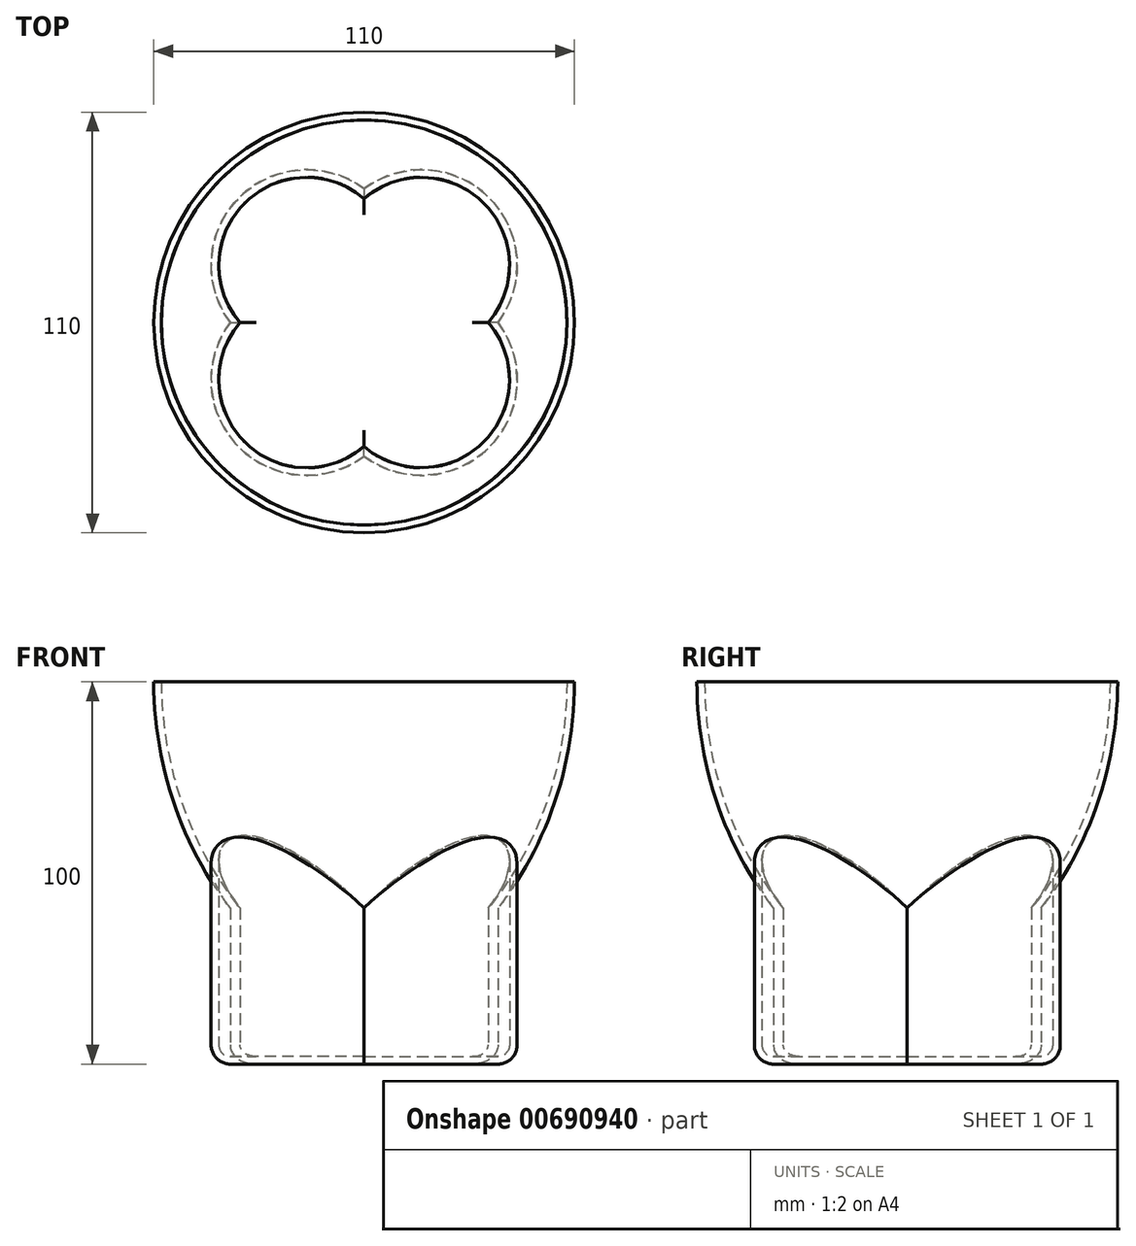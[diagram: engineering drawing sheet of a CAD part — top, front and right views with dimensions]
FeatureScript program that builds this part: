
annotation { "Feature Type Name" : "Feature", "Feature Type Description" : "" }
export const myFeature = defineFeature(function(context is Context, id is Id, definition is map)
    precondition{}
    {
        {
            var Q0;
            Q0=qCreatedBy(makeId("Top.planeOp"),FACE);
            var sketch = newSketch(context, id + "F0", { "sketchPlane" : qUnion([Q0])});
            skArc(sketch, "E0", {"start": v(0, 35) * mm, "mid": v(-32.68, 32.68) * mm, "end": v(-35, 0) * mm});
            skArc(sketch, "E1.MirrorC", {"start": v(0, 35) * mm, "mid": v(32.68, 32.68) * mm, "end": v(35, 0) * mm});
            skArc(sketch, "E2.trimOffspring", {"start": v(0, -35) * mm, "mid": v(-32.68, -32.68) * mm, "end": v(-35, 0) * mm});
            skArc(sketch, "E3.trimOffspring", {"start": v(0, -35) * mm, "mid": v(32.68, -32.68) * mm, "end": v(35, 0) * mm});
            skSolve(sketch);
        }
        {
            var Q0;
            Q0=qCreatedBy(makeId("Front.planeOp"),FACE);
            var sketch = newSketch(context, id + "F1", { "sketchPlane" : qUnion([Q0])});
            skFitSpline(sketch, "E4", {"points": [v(-55, 100) * mm, v(0, 20) * mm], "startDerivative": vector(0, -130.32) * mm, "endDerivative": vector(77.34, 0) * mm});
            skPoint(sketch, "E5", {"position": v(-33.03, 38.46) * mm});
            skLineSegment(sketch, "E6", {"start": v(-55, -8.59) * mm, "end": v(-55, 127.1) * mm, "construction": true});
            skLineSegment(sketch, "E7", {"start": v(-63.76, 20) * mm, "end": v(87.88, 20) * mm, "construction": true});
            skLineSegment(sketch, "E8", {"start": v(-55, 100) * mm, "end": v(0, 100) * mm});
            skLineSegment(sketch, "E9", {"start": v(0, 100) * mm, "end": v(0, 20) * mm});
            skLineSegment(sketch, "E10", {"start": v(0, 107.16) * mm, "end": v(0, -26.92) * mm, "construction": true});
            skPoint(sketch, "E10.endSnap0", {"position": v(0, 60) * mm});
            skSolve(sketch);
        }
        {
            var Q0;
            Q0 = qSketchRegion(id + "F1", true);
            var Q1;
            Q1=sQuery(id+"F1.wireOp",EDGE,"E10");
            revolve(context, id + "F2", {"entities" : qUnion([Q0]), "axis" : qUnion([Q1]), "revolveType" : RevolveType.FULL});
        }
        {
            var Q0;
            Q0 = qSketchRegion(id + "F0", true);
            extrude(context, id + "F3", {"entities" : qUnion([Q0]), "operationType" : NewBodyOperationType.ADD, "endBound" : BoundingType.UP_TO_NEXT, "depth" : 25 * mm, "offsetDistance" : 25 * mm});
        }
        {
            var Q0;
            Q0=makeQuery(id+"F3.opExtrude","CAP_EDGE",EDGE,{"disambiguationData":[OSD([sQuery(id+"F0.wireOp",EDGE,"E3.trimOffspring")])],"isStart":true});
            var Q1;
            Q1=makeQuery(id+"F3.opExtrude","CAP_EDGE",EDGE,{"disambiguationData":[OSD([sQuery(id+"F0.wireOp",EDGE,"E1.MirrorC")])],"isStart":true});
            var Q2;
            Q2=makeQuery(id+"F3.opExtrude","CAP_EDGE",EDGE,{"disambiguationData":[OSD([sQuery(id+"F0.wireOp",EDGE,"E0")])],"isStart":true});
            var Q3;
            Q3=makeQuery(id+"F3.opExtrude","CAP_EDGE",EDGE,{"disambiguationData":[OSD([sQuery(id+"F0.wireOp",EDGE,"E2.trimOffspring")])],"isStart":true});
            fillet(context, id + "F4", {"entities" : qUnion([Q0, Q1, Q2, Q3]), "radius" : 5 * mm, "tangentPropagation" : true, "allowEdgeOverflow" : false});
        }
        {
            var Q0;
            Q0=makeQuery(id+"F2.opRevolve","SWEPT_FACE",FACE,{"disambiguationData":[OSD([sQuery(id+"F1.wireOp",EDGE,"E8")])]});
            shell(context, id + "F5", {"entities" : qUnion([Q0]), "thickness" : 2 * mm});
        }
    });
